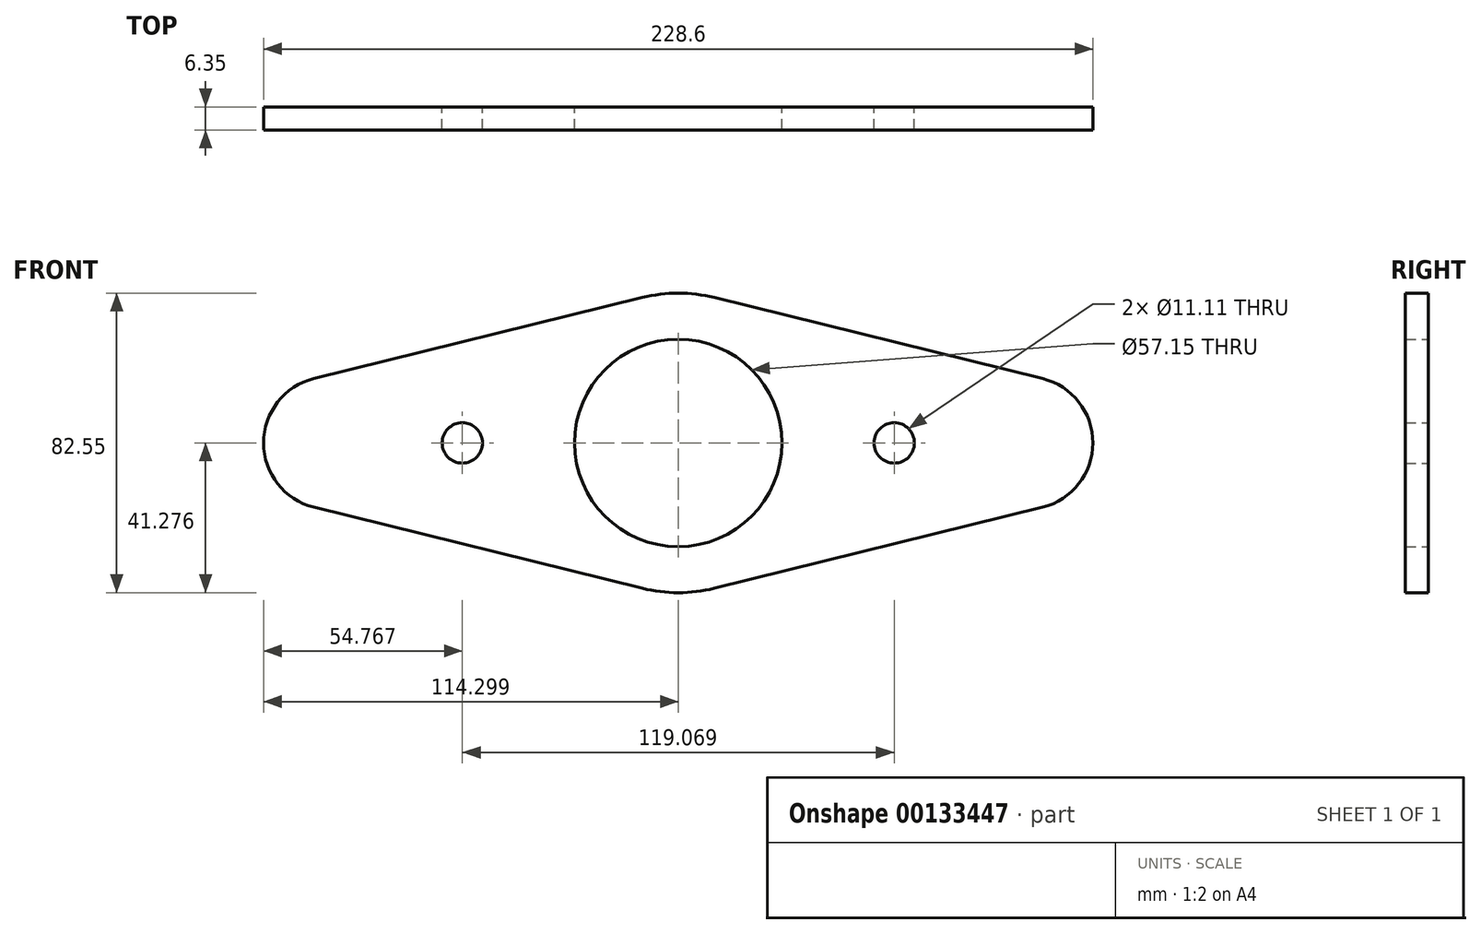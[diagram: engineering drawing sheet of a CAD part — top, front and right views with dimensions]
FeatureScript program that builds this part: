
annotation { "Feature Type Name" : "Feature", "Feature Type Description" : "" }
export const myFeature = defineFeature(function(context is Context, id is Id, definition is map)
    precondition{}
    {
        {
            var Q0;
            Q0=qCreatedBy(makeId("Front.planeOp"),FACE);
            var sketch = newSketch(context, id + "F0", { "sketchPlane" : qUnion([Q0])});
            skCircle(sketch, "E0", {"center": v(0, -2.05) * mm, "radius": 15.88 * mm});
            skCircle(sketch, "E1", {"center": v(0, -2.05) * mm, "radius": 28.58 * mm});
            skLineSegment(sketch, "E2", {"start": v(0, 26.52) * mm, "end": v(0, 39.22) * mm});
            skArc(sketch, "E3", {"start": v(-9.9, -42.13) * mm, "mid": v(0, -43.33) * mm, "end": v(9.9, -42.13) * mm});
            skLineSegment(sketch, "E4", {"start": v(-41.28, -2.05) * mm, "end": v(-53.98, -2.05) * mm});
            skCircle(sketch, "E5", {"center": v(-59.53, -2.05) * mm, "radius": 5.56 * mm});
            skCircle(sketch, "E6", {"center": v(59.54, -2.05) * mm, "radius": 5.56 * mm});
            skLineSegment(sketch, "E7", {"start": v(41.27, -2.05) * mm, "end": v(53.97, -2.05) * mm});
            skLineSegment(sketch, "E8", {"start": v(-65.09, -2.05) * mm, "end": v(-77.79, -2.05) * mm});
            skArc(sketch, "E9", {"start": v(-100.42, 15.67) * mm, "mid": v(-114.3, -2.05) * mm, "end": v(-100.42, -19.78) * mm});
            skLineSegment(sketch, "E10", {"start": v(65.1, -2.05) * mm, "end": v(77.8, -2.05) * mm});
            skArc(sketch, "E11", {"start": v(100.42, -19.78) * mm, "mid": v(114.3, -2.05) * mm, "end": v(100.42, 15.67) * mm});
            skLineSegment(sketch, "E12", {"start": v(-100.42, 15.67) * mm, "end": v(-9.9, 38.02) * mm});
            skLineSegment(sketch, "E13", {"start": v(9.9, 38.02) * mm, "end": v(100.42, 15.67) * mm});
            skLineSegment(sketch, "E14", {"start": v(-100.42, -19.78) * mm, "end": v(-9.9, -42.13) * mm});
            skLineSegment(sketch, "E15", {"start": v(100.42, -19.78) * mm, "end": v(9.9, -42.13) * mm});
            skArc(sketch, "E16.trimOffspring", {"start": v(9.9, 38.02) * mm, "mid": v(0, 39.22) * mm, "end": v(-9.9, 38.02) * mm});
            skSolve(sketch);
        }
        {
            var Q0;
            Q0=makeQuery(id+"F0.imprint","IMPRINT",FACE,{"disambiguationData":[TD([[makeQuery(id+"F0.imprint","IMPRINT",EDGE,{"derivedFrom":sQuery(id+"F0.wireOp",EDGE,"E1")}),-1.0]])]});
            extrude(context, id + "F1", {"entities" : qUnion([Q0]), "depth" : 6.35 * mm});
        }
    });
